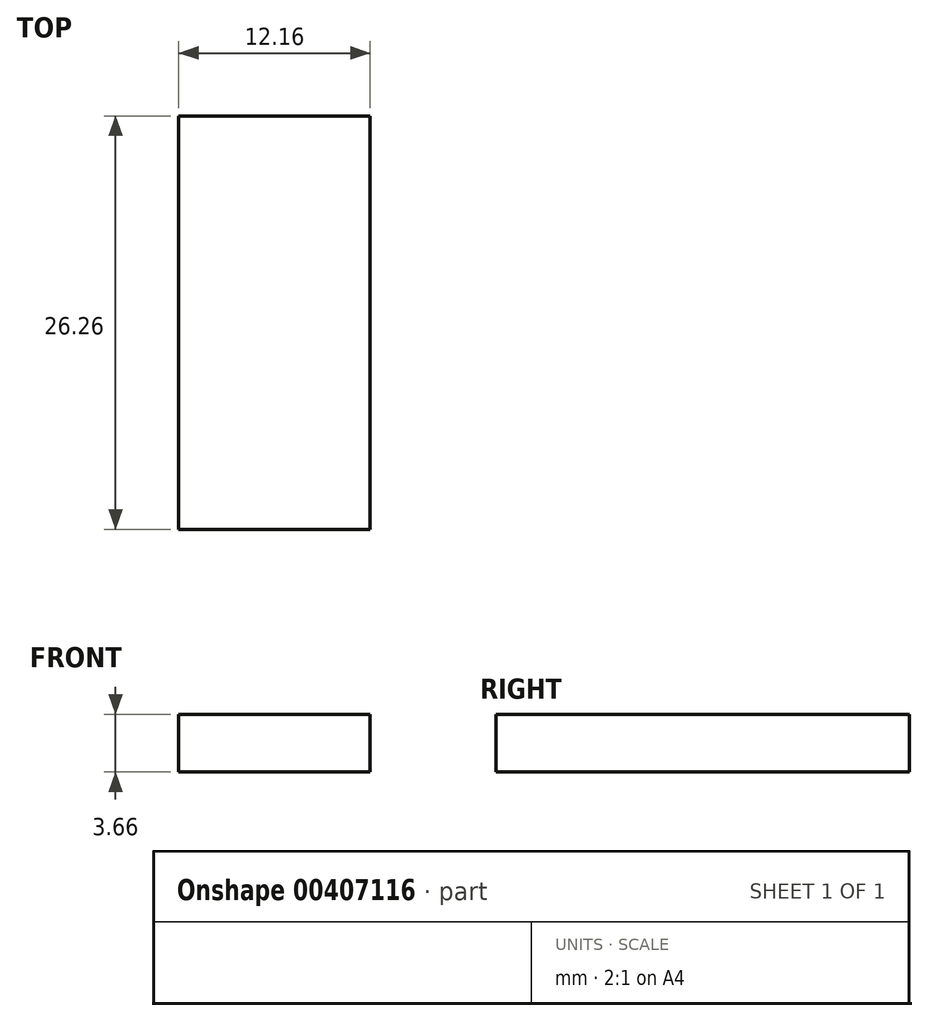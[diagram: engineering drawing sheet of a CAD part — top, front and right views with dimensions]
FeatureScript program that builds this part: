
annotation { "Feature Type Name" : "Feature", "Feature Type Description" : "" }
export const myFeature = defineFeature(function(context is Context, id is Id, definition is map)
    precondition{}
    {
        {
            var Q0;
            Q0=qCreatedBy(makeId("Right.planeOp"),FACE);
            var sketch = newSketch(context, id + "F0", { "sketchPlane" : qUnion([Q0])});
            skLineSegment(sketch, "E0.bottom", {"start": v(26.26, 0) * mm, "end": v(0, 0) * mm});
            skLineSegment(sketch, "E0.top", {"start": v(26.26, 3.66) * mm, "end": v(0, 3.66) * mm});
            skLineSegment(sketch, "E0.left", {"start": v(26.26, 0) * mm, "end": v(26.26, 3.66) * mm});
            skLineSegment(sketch, "E0.right", {"start": v(0, 0) * mm, "end": v(0, 3.66) * mm});
            skSolve(sketch);
        }
        {
            var Q0;
            Q0=makeQuery(id+"F0.imprint","IMPRINT",FACE,{"disambiguationData":[TD([[makeQuery(id+"F0.imprint","IMPRINT",EDGE,{"derivedFrom":sQuery(id+"F0.wireOp",EDGE,"E0.bottom")}),-1.0]])]});
            extrude(context, id + "F1", {"entities" : qUnion([Q0]), "depth" : 12.16 * mm});
        }
    });
